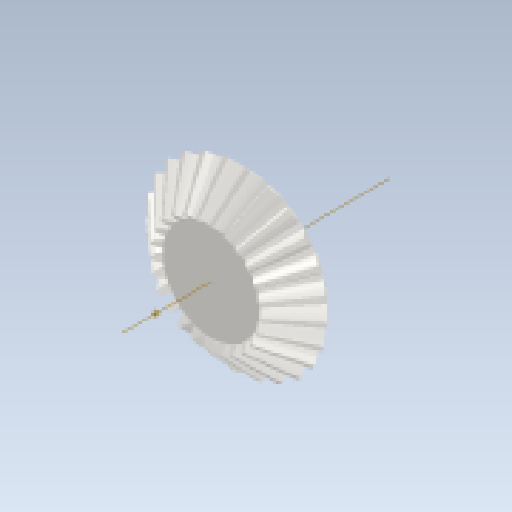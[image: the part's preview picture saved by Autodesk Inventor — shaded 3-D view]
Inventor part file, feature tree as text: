
AUTODESK INVENTOR PART (.ipt)
format: ipt  version: 2023 (Build 270158000, 158)  size: 540,672 bytes
history: native  units: mm
features: other x24, loft x2, pattern_circular x2, sketch x1
ambient origin geometry x6: Origin, XZ Plane, X Axis, Y Axis, Z Axis, Center Point
bodies: Solid1 (feature_tree)
feature tree (29):
  other  "Top Point"
  other  "Mesh Plane2"
  other  "Teeth Body"
  other  "Start Point"
  other  "Tooth Plane"
  other  "Start Sketch"
  other  "End Point"
  other  "3D Sketch Right"
  other  "End Plane Right"
  loft  "Loft Right"
  pattern_circular  "Circular Pattern Right"  [2 undecoded]
  other  "3D Sketch Left"
  other  "End Plane Left"
  loft  "Loft Left"
  pattern_circular  "Circular Pattern Left"  [2 undecoded]
  other  "Fix Body"
  other  "Mesh Plane"
  other  "Top Plane"
  other  "Teeth Body Sketch"
  other  "End Plane"
  other  "End Sketch"
  other  "Helical Curve Left"
  other  "End Sketch Left"
  other  "Body Sketch"
  sketch  "Sketch6"  dims[d0=25.4mm d1=23.675791mm d2=26.836841mm d3=7.1mm d4=11.98158mm d5=90.0deg d7=6.490689mm d8=6.790786mm d9=15.450402mm d11=7.21176mm d12=3.884455mm d15=4.064053mm d16=9.246537mm d17=0.0mm d18=90.0deg d19=0.0mm d20=90.0deg d21=250.0mm d22=360.0deg d26=124.383686mm d27=5.099484mm d28=25.4mm d29=-7.853982mm d30=3.884455mm d31=4.064053mm d32=9.246537mm d35=0.0mm d37=0.0mm d39=0.0mm d40=90.0deg d41=250.0mm d42=360.0deg d46=90.0deg d47=90.0deg d48=0.0mm d49=0.0mm d50=90.0deg d51=1.256637mm d52=0.0mm d53=0.0mm d54=0.0mm d56=5.737655mm d57=19.647072mm d58=16.473088mm d59=11.758101mm d60=9.85858mm d61=11.758101mm d62=9.85858mm d63=90.0deg d64=90.0deg d65=124.383686mm d66=31.5mm d67=25.4mm d68=-7.853982mm d69=5.099484mm d70=4.064053mm d71=9.246537mm d72=3.884455mm d73=9.85858mm d74=11.758101mm d75=0.0mm d76=90.0deg d77=0.0mm d78=90.0deg d79=0.0mm d80=90.0deg d81=250.0mm d82=360.0deg d84=10.0mm d85=20.0mm d86=20.0mm d87=10.0mm d88=0.0mm d89=0.0mm]
  other  "Srf1"
  other  "Helical Curve Right"
  other  "End Sketch Right"
  other  "Pitch Diameter"
note: 4 required parameter values undecoded (feature->parameter linkage not recoverable at this tier; creation-order binding heuristic only, values carry confidence <= 0.55)
